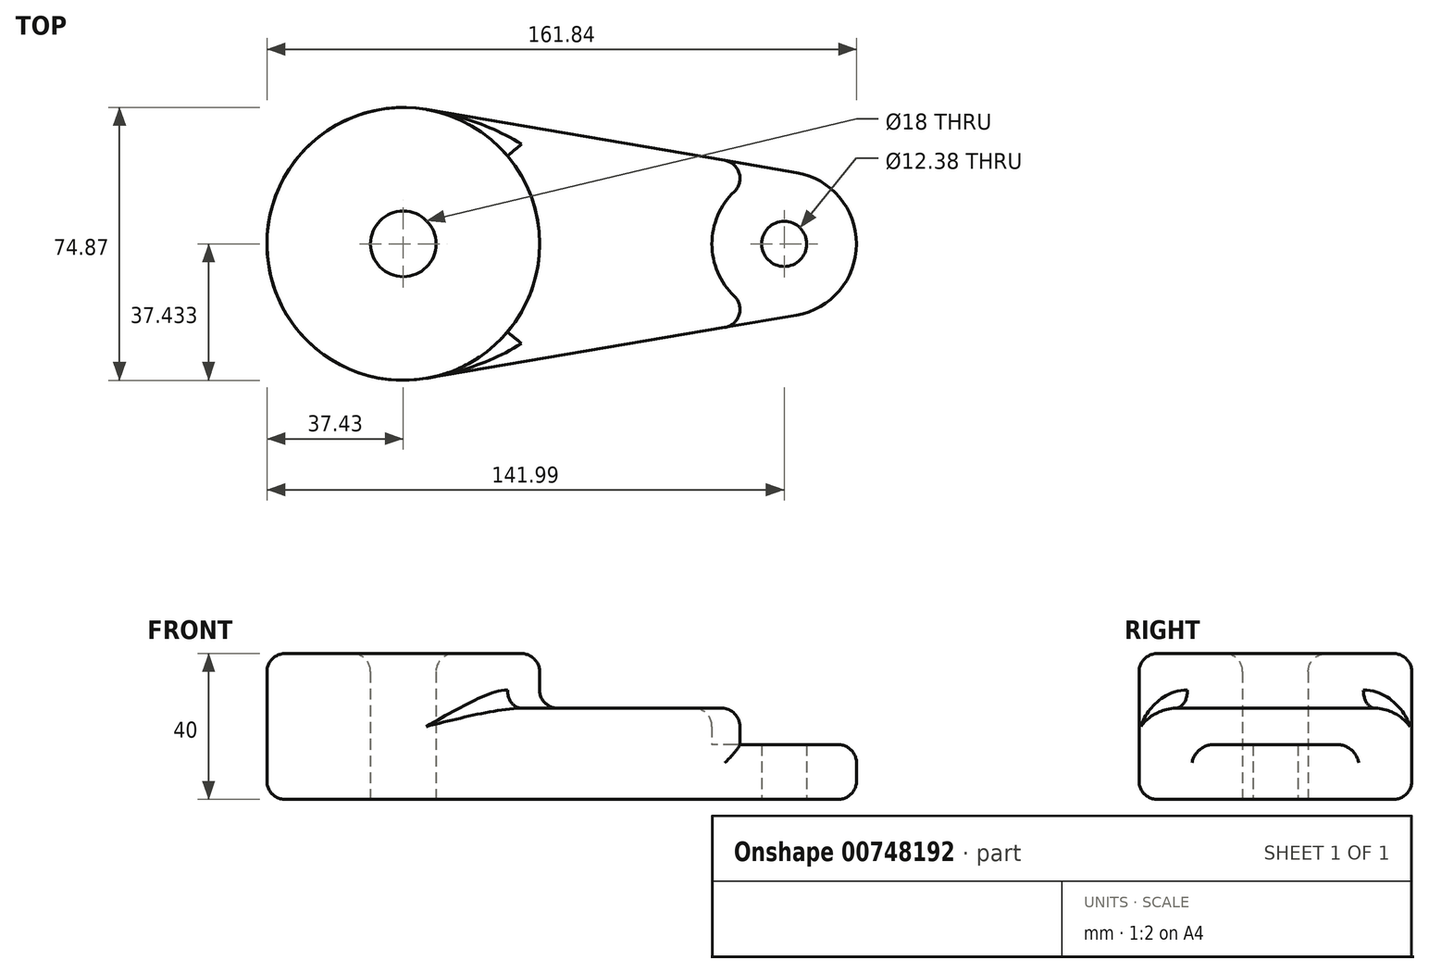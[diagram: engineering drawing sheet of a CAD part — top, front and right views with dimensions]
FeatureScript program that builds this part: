
annotation { "Feature Type Name" : "Feature", "Feature Type Description" : "" }
export const myFeature = defineFeature(function(context is Context, id is Id, definition is map)
    precondition{}
    {
        {
            var Q0;
            Q0=qCreatedBy(makeId("Top.planeOp"),FACE);
            var sketch = newSketch(context, id + "F0", { "sketchPlane" : qUnion([Q0])});
            skCircle(sketch, "E0", {"center": v(-62.4, 21.6) * mm, "radius": 9 * mm});
            skCircle(sketch, "E1", {"center": v(-62.4, 21.6) * mm, "radius": 37.43 * mm});
            skCircle(sketch, "E2", {"center": v(42.16, 21.6) * mm, "radius": 6.2 * mm});
            skCircle(sketch, "E3", {"center": v(42.16, 21.6) * mm, "radius": 19.85 * mm});
            skLineSegment(sketch, "E4", {"start": v(-56.1, 58.5) * mm, "end": v(45.5, 41.17) * mm});
            skLineSegment(sketch, "E5", {"start": v(-56.1, -15.3) * mm, "end": v(45.5, 2.04) * mm});
            skSolve(sketch);
        }
        {
            var Q0;
            Q0=makeQuery(id+"F0.imprint","IMPRINT",FACE,{"disambiguationData":[TD([[makeQuery(id+"F0.imprint","IMPRINT",EDGE,{"derivedFrom":sQuery(id+"F0.wireOp",EDGE,"E0")}),-1.0]])]});
            extrude(context, id + "F1", {"entities" : qUnion([Q0]), "depth" : 40 * mm, "offsetDistance" : 25 * mm});
        }
        {
            var Q0;
            {var subQ0=sQuery(id+"F0.wireOp",EDGE,"E4");Q0=makeQuery(id+"F0.imprint","IMPRINT",FACE,{"disambiguationData":[TD([[makeQuery(id+"F0.imprint","IMPRINT",EDGE,{"derivedFrom":subQ0}),-1.0]])]});}
            extrude(context, id + "F2", {"entities" : qUnion([Q0]), "operationType" : NewBodyOperationType.ADD, "depth" : 25 * mm, "offsetDistance" : 25 * mm});
        }
        {
            var Q0;
            Q0=makeQuery(id+"F0.imprint","IMPRINT",FACE,{"disambiguationData":[TD([[makeQuery(id+"F0.imprint","IMPRINT",EDGE,{"derivedFrom":sQuery(id+"F0.wireOp",EDGE,"E2")}),-1.0]])]});
            extrude(context, id + "F3", {"entities" : qUnion([Q0]), "operationType" : NewBodyOperationType.ADD, "depth" : 15 * mm, "offsetDistance" : 25 * mm});
        }
        {
            var Q0;
            Q0=makeQuery(id+"F1.opExtrude","CAP_FACE",FACE,{"disambiguationData":[OSD([sQuery(id+"F0.wireOp",EDGE,"E0"),sQuery(id+"F0.wireOp",EDGE,"E1")])],"isStart":false});
            var Q1;
            Q1=makeQuery(id+"F2.opExtrude","CAP_FACE",FACE,{"disambiguationData":[OSD([sQuery(id+"F0.wireOp",EDGE,"E1"),sQuery(id+"F0.wireOp",EDGE,"E3"),sQuery(id+"F0.wireOp",EDGE,"E4"),sQuery(id+"F0.wireOp",EDGE,"E5")])],"isStart":false});
            var Q2;
            Q2=makeQuery(id+"F2.opExtrude","SWEPT_FACE",FACE,{"disambiguationData":[OSD([sQuery(id+"F0.wireOp",EDGE,"E5")])]});
            var Q3;
            Q3=makeQuery(id+"F2.opExtrude","SWEPT_FACE",FACE,{"disambiguationData":[OSD([sQuery(id+"F0.wireOp",EDGE,"E4")])]});
            var Q4;
            Q4=makeQuery(id+"F3.opExtrude","SWEPT_FACE",FACE,{"disambiguationData":[OSD([sQuery(id+"F0.wireOp",EDGE,"E3")])]});
            fillet(context, id + "F4", {"entities" : qUnion([Q0, Q1, Q2, Q3, Q4]), "radius" : 5 * mm, "tangentPropagation" : true, "allowEdgeOverflow" : false});
        }
    });
